# Revit family: 306_cddfc1bd8b7649d3add90f0bde6465
name_source: partatom
category: Pipe Accessories
units: mm (PartAtom-declared; Revit-internal decimal feet)

## family parameters
Always vertical = Yes
Cut with Voids When Loaded = No
Part Type = Valve - Breaks Into
Round Connector Dimension = Use Diameter
Shared = No
Work Plane-Based = No

## types (4) — shared parameters
AL1 = 100 mm
AL2 = 58 mm
AL3 = 128 mm
AL3__ve = -128 mm  [stored -0.419948 ft]
ALR = 16 mm
ALR__ve = -16 mm  [stored -0.0524934 ft]
CC = 71 mm
CC1 = 45 mm
CC1__ve = -45 mm  [stored -0.147638 ft]
CenSd_RNR_6 = 7 mm  [stored 0.0229659 ft]
Description = Chr.-plated 2-way zone valve, 230V actuator, M-M connections
G1 = 31 mm  [stored 0.101706 ft]
G2 = 44 mm
GG = 58 mm
GG__ve = -58 mm  [stored -0.190289 ft]
KLR = 12 mm  [stored 0.0393701 ft]
KT = 22 mm  [stored 0.0721785 ft]
KT1 = 18 mm
KT11 = 16 mm
L2D = 175 mm
L2D_Min = 3048 mm
Manufacturer = FAR
QmdConnectorList = 301;D;302;D
RH = 4 mm  [stored 0.0131234 ft]
RNR = 8 mm  [stored 0.0262467 ft]
RW = 6 mm  [stored 0.019685 ft]
TRH = 6 mm  [stored 0.019685 ft]
TS = 13 mm  [stored 0.0426509 ft]
TS__ve = -13 mm  [stored -0.0426509 ft]
W2D = 40 mm  [stored 0.131234 ft]
magiPartTypeId = 306
magiProductFamilyId = cddfc1bd8b7649d3add90f0bde6465

## per-type parameters (varying)
- 303915 112 30: B0=37 mm; B1=5 mm  [stored 0.0164042 ft]; B2=11 mm; B22=9 mm  [stored 0.0295276 ft]; BR=19 mm  [stored 0.062336 ft]; BR1=15 mm  [stored 0.0492126 ft]; CenSd_NR1_6=26 mm; CenSd_NRS1_6=9 mm  [stored 0.0295276 ft]; CenSd_NR_6=30 mm  [stored 0.0984252 ft]; D=40 mm; L1=9 mm  [stored 0.0295276 ft]; L1__ve=-9 mm; L2=88 mm; LR=53 mm; LR__ve=-53 mm; NR=35 mm  [stored 0.114829 ft]; NR1=30 mm  [stored 0.0984252 ft]; NR2=35 mm  [stored 0.114829 ft]; NRS1=10 mm  [stored 0.0328084 ft]; NT=18 mm; NT__ve=-18 mm; R=20 mm  [stored 0.0656168 ft]; RT=24 mm  [stored 0.0787402 ft]; RT1=29 mm  [stored 0.0951444 ft]; RT2=32 mm; magiProductId=a51f1d55bbc74f8bbc3cfa2ffd542c
- 303915 112 80: B0=37 mm; B1=5 mm  [stored 0.0164042 ft]; B2=11 mm; B22=9 mm  [stored 0.0295276 ft]; BR=19 mm  [stored 0.062336 ft]; BR1=15 mm  [stored 0.0492126 ft]; CenSd_NR1_6=26 mm; CenSd_NRS1_6=9 mm  [stored 0.0295276 ft]; CenSd_NR_6=30 mm  [stored 0.0984252 ft]; D=40 mm; L1=9 mm  [stored 0.0295276 ft]; L1__ve=-9 mm; L2=88 mm; LR=53 mm; LR__ve=-53 mm; NR=35 mm  [stored 0.114829 ft]; NR1=30 mm  [stored 0.0984252 ft]; NR2=35 mm  [stored 0.114829 ft]; NRS1=10 mm  [stored 0.0328084 ft]; NT=18 mm; NT__ve=-18 mm; R=20 mm  [stored 0.0656168 ft]; RT=24 mm  [stored 0.0787402 ft]; RT1=29 mm  [stored 0.0951444 ft]; RT2=32 mm; magiProductId=ff09f41977944c23b1345aac47e2f7
- 303915 2 30: B0=45 mm; B1=6 mm  [stored 0.019685 ft]; B2=10 mm  [stored 0.0328084 ft]; B22=8 mm  [stored 0.0262467 ft]; BR=24 mm  [stored 0.0787402 ft]; BR1=19 mm  [stored 0.062336 ft]; CenSd_NR1_6=32 mm; CenSd_NRS1_6=11 mm; CenSd_NR_6=38 mm  [stored 0.124672 ft]; D=50 mm; L1=10 mm  [stored 0.0328084 ft]; L1__ve=-10 mm  [stored -0.0328084 ft]; L2=101 mm; LR=64 mm; LR__ve=-64 mm; NR=44 mm; NR1=38 mm  [stored 0.124672 ft]; NR2=43 mm; NRS1=13 mm  [stored 0.0426509 ft]; NT=20 mm  [stored 0.0656168 ft]; NT__ve=-20 mm; R=25 mm  [stored 0.082021 ft]; RT=30 mm  [stored 0.0984252 ft]; RT1=36 mm; RT2=39 mm; magiProductId=67f49cb8cb794e439dfa3792955884
- 303915 2 80: B0=45 mm; B1=6 mm  [stored 0.019685 ft]; B2=10 mm  [stored 0.0328084 ft]; B22=8 mm  [stored 0.0262467 ft]; BR=24 mm  [stored 0.0787402 ft]; BR1=19 mm  [stored 0.062336 ft]; CenSd_NR1_6=32 mm; CenSd_NRS1_6=11 mm; CenSd_NR_6=38 mm  [stored 0.124672 ft]; D=50 mm; L1=10 mm  [stored 0.0328084 ft]; L1__ve=-10 mm  [stored -0.0328084 ft]; L2=101 mm; LR=64 mm; LR__ve=-64 mm; NR=44 mm; NR1=38 mm  [stored 0.124672 ft]; NR2=43 mm; NRS1=13 mm  [stored 0.0426509 ft]; NT=20 mm  [stored 0.0656168 ft]; NT__ve=-20 mm; R=25 mm  [stored 0.082021 ft]; RT=30 mm  [stored 0.0984252 ft]; RT1=36 mm; RT2=39 mm; magiProductId=179d64de5f9f42c0b12d5df99a2db0

note: column(s) folded — value = type name in every type: MC Product Code

note: [stored X ft] marks values corroborated as IEEE doubles in the binary element streams (Revit-internal decimal feet)

## geometry (parser evidence)
native form markers: Sweep x2
no freeform markers — native parametric forms only
